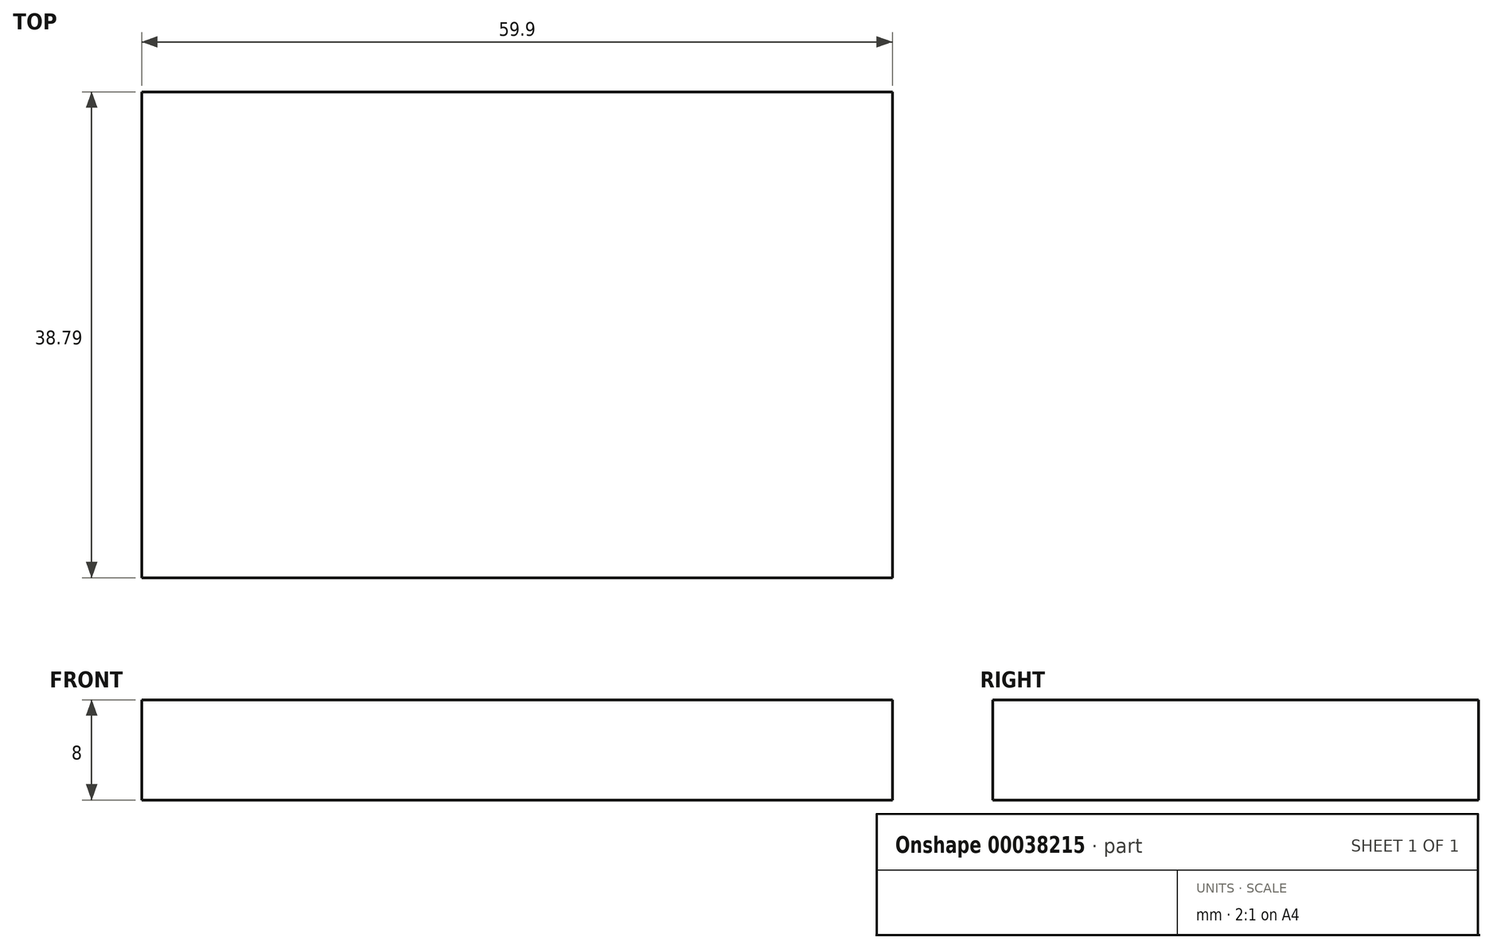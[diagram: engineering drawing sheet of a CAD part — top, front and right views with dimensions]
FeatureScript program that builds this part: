
annotation { "Feature Type Name" : "Feature", "Feature Type Description" : "" }
export const myFeature = defineFeature(function(context is Context, id is Id, definition is map)
    precondition{}
    {
        {
            var Q0;
            Q0=qCreatedBy(makeId("Top.planeOp"),FACE);
            var sketch = newSketch(context, id + "F0", { "sketchPlane" : qUnion([Q0])});
            skLineSegment(sketch, "E0.bottom", {"start": v(-26.81, -19.82) * mm, "end": v(33.09, -19.82) * mm});
            skLineSegment(sketch, "E0.top", {"start": v(-26.81, 18.97) * mm, "end": v(33.09, 18.97) * mm});
            skLineSegment(sketch, "E0.left", {"start": v(-26.81, -19.82) * mm, "end": v(-26.81, 18.97) * mm});
            skLineSegment(sketch, "E0.right", {"start": v(33.09, -19.82) * mm, "end": v(33.09, 18.97) * mm});
            skSolve(sketch);
        }
        {
            var Q0;
            Q0 = qSketchRegion(id + "F0", true);
            extrude(context, id + "F1", {"entities" : qUnion([Q0]), "depth" : 8 * mm});
        }
        {
            var Q0;
            Q0=makeQuery(id+"F1.opExtrude","CAP_FACE",FACE,{"disambiguationData":[OSD([sQuery(id+"F0.wireOp",EDGE,"E0.bottom"),sQuery(id+"F0.wireOp",EDGE,"E0.top"),sQuery(id+"F0.wireOp",EDGE,"E0.left"),sQuery(id+"F0.wireOp",EDGE,"E0.right")])],"isStart":false});
            cPlane(context, id + "F2", {"entities" : qUnion([Q0]), "cplaneType" : CPlaneType.OFFSET, "offset" : 8 * mm, "width" : 152.4 * mm, "height" : 152.4 * mm});
        }
    });
